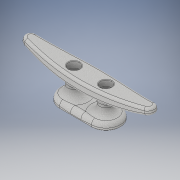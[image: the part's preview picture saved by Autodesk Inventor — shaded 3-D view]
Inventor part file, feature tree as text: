
AUTODESK INVENTOR PART (.ipt)
format: ipt  version: 2018 (Build 220112000, 112)  size: 919,552 bytes
history: native  units: in
note: dims shown in document units (in); Inventor stores cm internally (conversion verified against a paired STEP export)
features: mirror x1
ambient origin geometry x8: Origin, YZ Plane, XZ Plane, XY Plane, X Axis, Y Axis, Z Axis, Center Point
bodies: Solid1 (feature_tree)
feature tree (1):
  mirror  "Mirror2"
